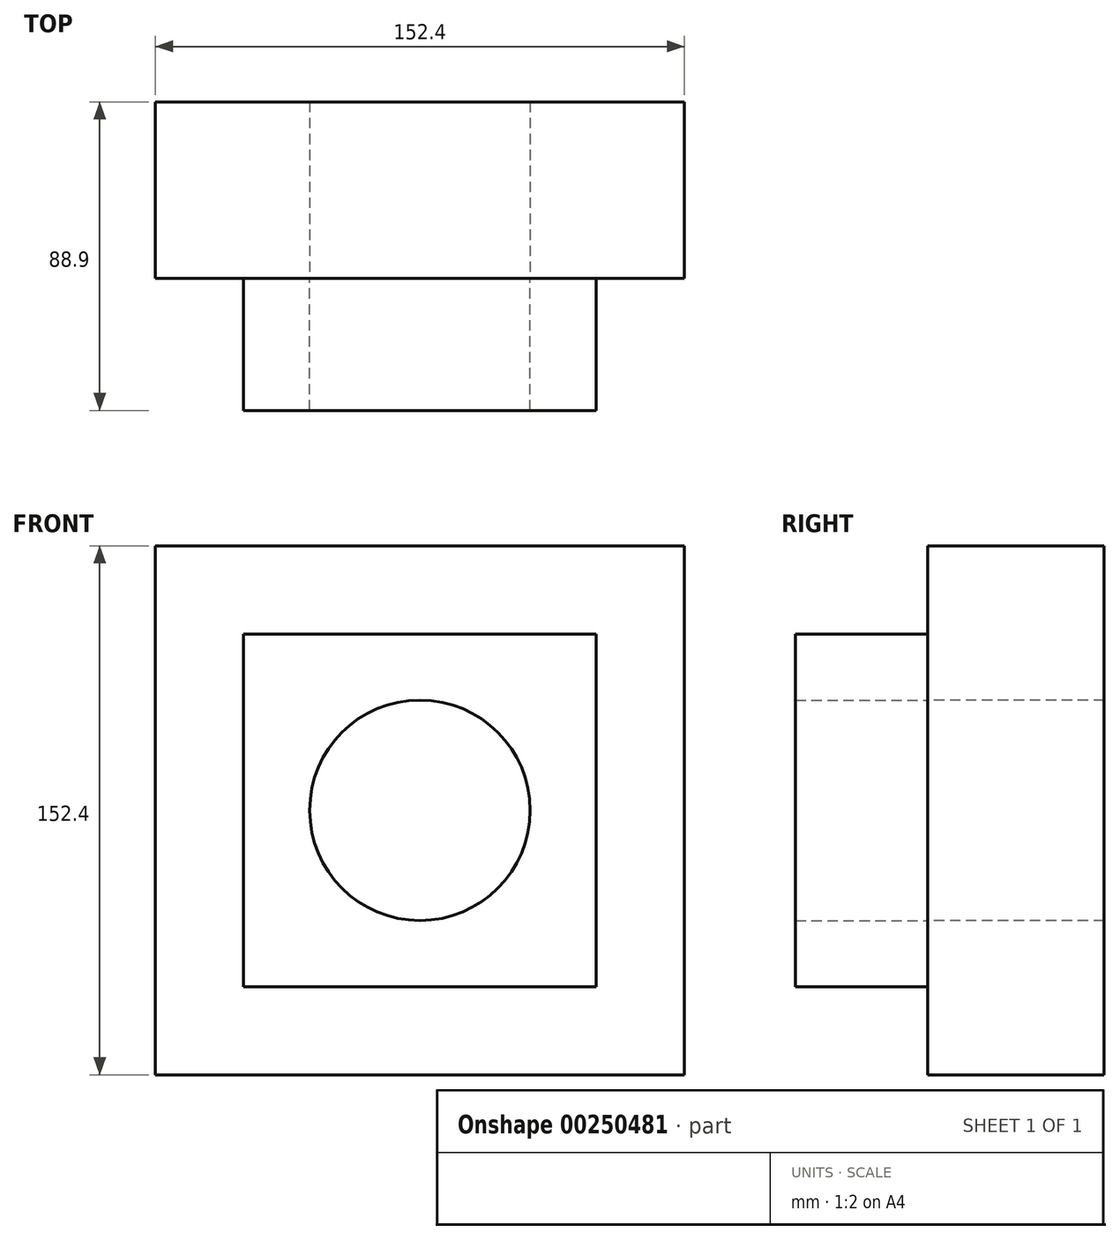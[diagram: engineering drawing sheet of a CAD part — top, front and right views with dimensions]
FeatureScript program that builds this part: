
annotation { "Feature Type Name" : "Feature", "Feature Type Description" : "" }
export const myFeature = defineFeature(function(context is Context, id is Id, definition is map)
    precondition{}
    {
        {
            var Q0;
            Q0=qCreatedBy(makeId("Front.planeOp"),FACE);
            var sketch = newSketch(context, id + "F0", { "sketchPlane" : qUnion([Q0])});
            skCircle(sketch, "E0", {"center": v(0, 0) * mm, "radius": 31.75 * mm});
            skLineSegment(sketch, "E1.bottom", {"start": v(50.8, 50.8) * mm, "end": v(-50.8, 50.8) * mm});
            skLineSegment(sketch, "E1.top", {"start": v(50.8, -50.8) * mm, "end": v(-50.8, -50.8) * mm});
            skLineSegment(sketch, "E1.left", {"start": v(50.8, 50.8) * mm, "end": v(50.8, -50.8) * mm});
            skLineSegment(sketch, "E1.right", {"start": v(-50.8, 50.8) * mm, "end": v(-50.8, -50.8) * mm});
            skLineSegment(sketch, "E2.bottom", {"start": v(76.2, -76.2) * mm, "end": v(-76.2, -76.2) * mm});
            skLineSegment(sketch, "E2.top", {"start": v(76.2, 76.2) * mm, "end": v(-76.2, 76.2) * mm});
            skLineSegment(sketch, "E2.left", {"start": v(76.2, -76.2) * mm, "end": v(76.2, 76.2) * mm});
            skLineSegment(sketch, "E2.right", {"start": v(-76.2, -76.2) * mm, "end": v(-76.2, 76.2) * mm});
            skSolve(sketch);
        }
        {
            var Q0;
            Q0=makeQuery(id+"F0.imprint","IMPRINT",FACE,{"disambiguationData":[TD([[makeQuery(id+"F0.imprint","IMPRINT",EDGE,{"derivedFrom":sQuery(id+"F0.wireOp",EDGE,"E0")}),-1.0]])]});
            extrude(context, id + "F1", {"entities" : qUnion([Q0]), "depth" : 38.1 * mm});
        }
        {
            var Q0;
            Q0 = qSketchRegion(id + "F0", true);
            var Q1;
            Q1=makeQuery(id+"F0.imprint","IMPRINT",FACE,{"disambiguationData":[TD([[makeQuery(id+"F0.imprint","IMPRINT",EDGE,{"derivedFrom":sQuery(id+"F0.wireOp",EDGE,"E0")}),-1.0]])]});
            extrude(context, id + "F2", {"entities" : qUnion([Q0, Q1]), "oppositeDirection" : true, "depth" : 50.8 * mm});
        }
    });
